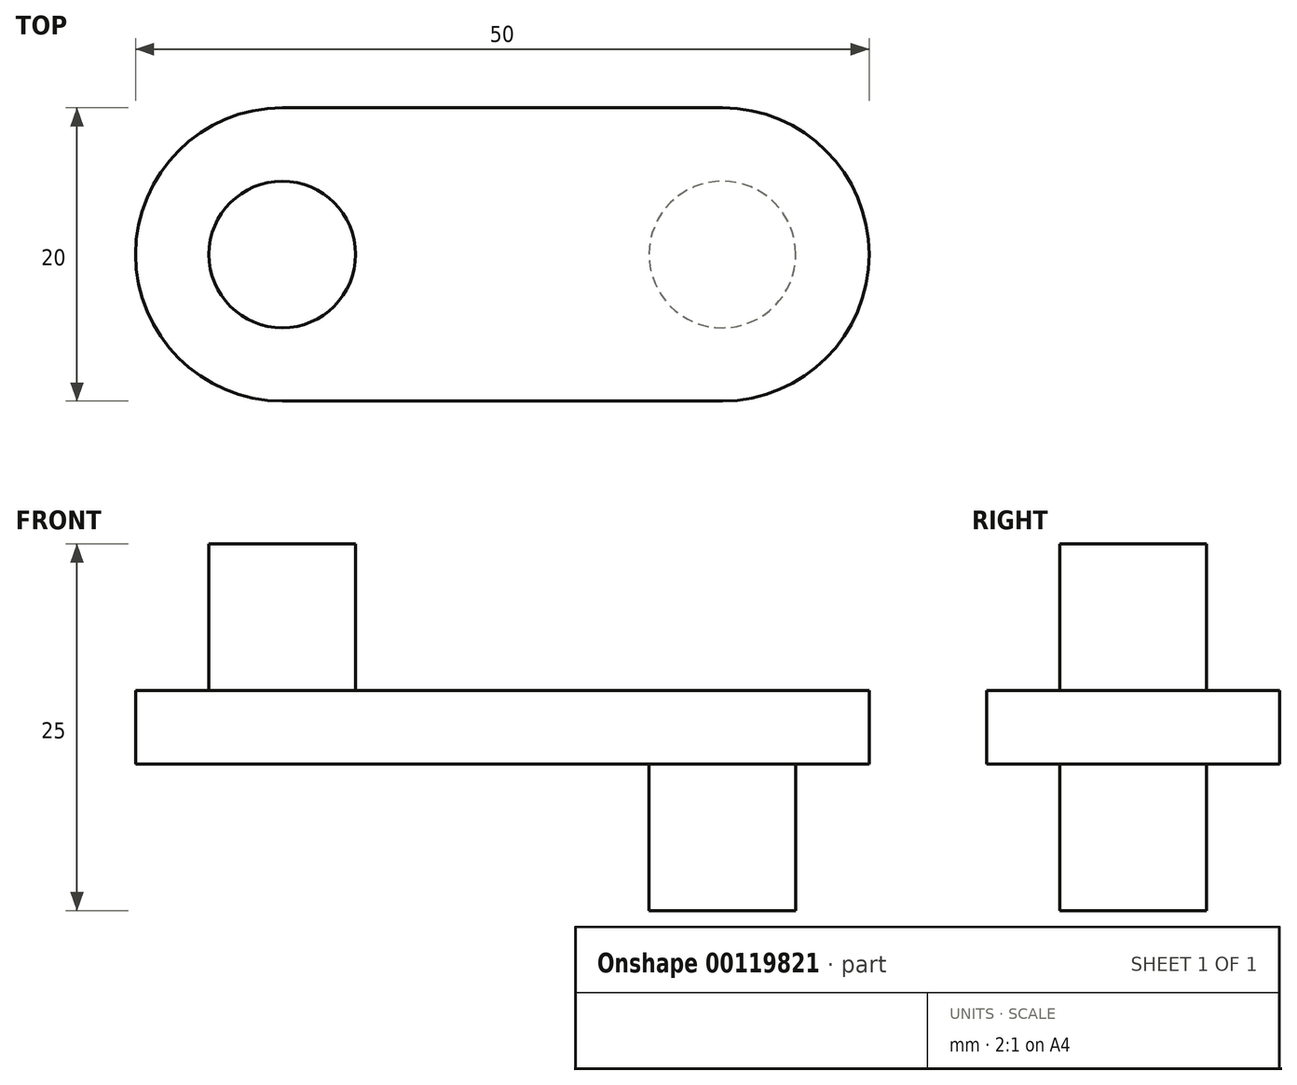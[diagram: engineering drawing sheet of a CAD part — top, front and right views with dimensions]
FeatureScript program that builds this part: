
annotation { "Feature Type Name" : "Feature", "Feature Type Description" : "" }
export const myFeature = defineFeature(function(context is Context, id is Id, definition is map)
    precondition{}
    {
        {
            var Q0;
            Q0=qCreatedBy(makeId("Top.planeOp"),FACE);
            var sketch = newSketch(context, id + "F0", { "sketchPlane" : qUnion([Q0])});
            skLineSegment(sketch, "E0.bottom", {"start": v(0, 0) * mm, "end": v(30, 0) * mm});
            skLineSegment(sketch, "E0.top", {"start": v(0, 20) * mm, "end": v(30, 20) * mm});
            skArc(sketch, "E1", {"start": v(0, 20) * mm, "mid": v(-10, 10) * mm, "end": v(0, 0) * mm});
            skArc(sketch, "E2", {"start": v(30, 0) * mm, "mid": v(40, 10) * mm, "end": v(30, 20) * mm});
            skCircle(sketch, "E3", {"center": v(0, 10) * mm, "radius": 5 * mm});
            skCircle(sketch, "E4", {"center": v(30, 10) * mm, "radius": 5 * mm});
            skSolve(sketch);
        }
        {
            var Q0;
            Q0 = qSketchRegion(id + "F0", true);
            var Q1;
            Q1=makeQuery(id+"F0.imprint","IMPRINT",FACE,{"disambiguationData":[TD([[makeQuery(id+"F0.imprint","IMPRINT",EDGE,{"derivedFrom":sQuery(id+"F0.wireOp",EDGE,"E0.bottom")}),1.0]])]});
            extrude(context, id + "F1", {"entities" : qUnion([Q0, Q1]), "depth" : 5 * mm});
        }
        {
            var Q0;
            Q0=makeQuery(id+"F0.imprint","IMPRINT",FACE,{"disambiguationData":[TD([[makeQuery(id+"F0.imprint","IMPRINT",EDGE,{"derivedFrom":sQuery(id+"F0.wireOp",EDGE,"E3")}),1.0]])]});
            extrude(context, id + "F2", {"entities" : qUnion([Q0]), "operationType" : NewBodyOperationType.ADD, "depth" : 15 * mm});
        }
        {
            var Q0;
            Q0=makeQuery(id+"F0.imprint","IMPRINT",FACE,{"disambiguationData":[TD([[makeQuery(id+"F0.imprint","IMPRINT",EDGE,{"derivedFrom":sQuery(id+"F0.wireOp",EDGE,"E4")}),1.0]])]});
            extrude(context, id + "F3", {"entities" : qUnion([Q0]), "operationType" : NewBodyOperationType.ADD, "oppositeDirection" : true, "depth" : 10 * mm, "hasSecondDirection" : true, "secondDirectionOppositeDirection" : false, "secondDirectionDepth" : 5 * mm});
        }
    });
